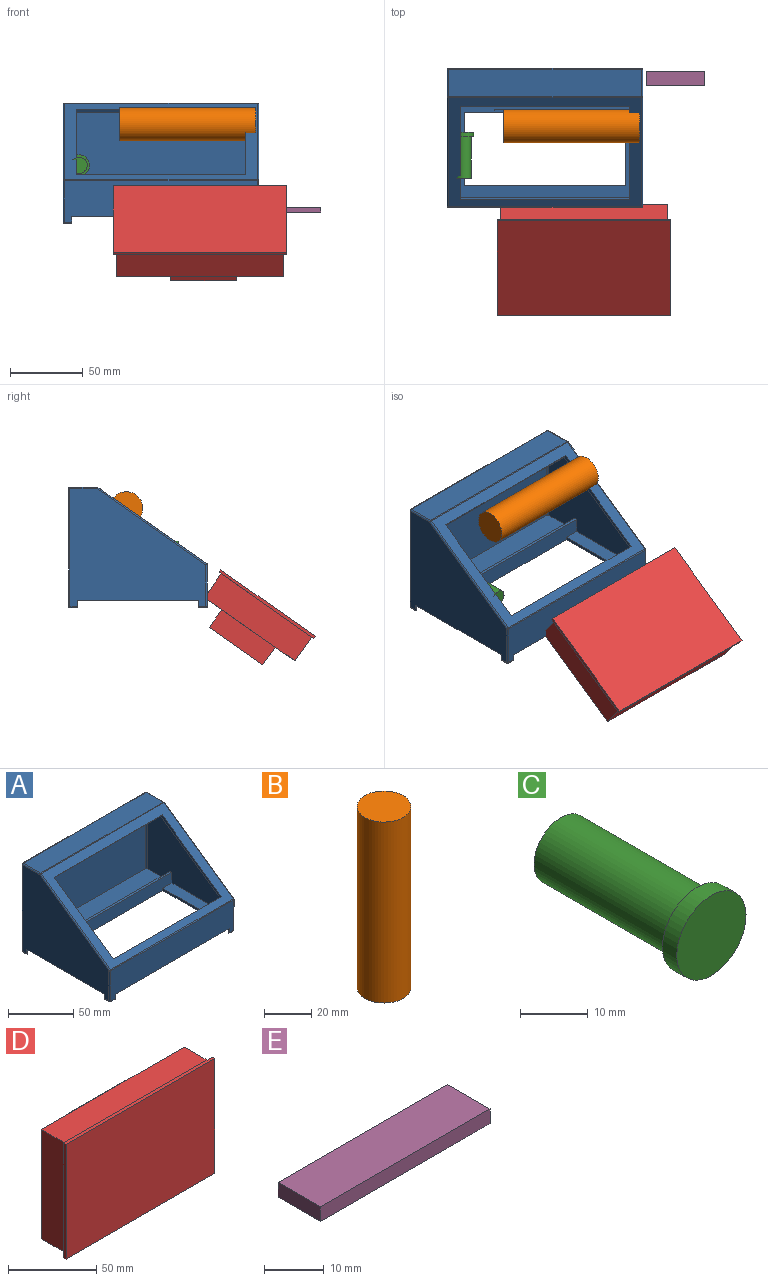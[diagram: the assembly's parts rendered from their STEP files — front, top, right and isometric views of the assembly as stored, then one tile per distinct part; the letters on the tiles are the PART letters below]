
ASSEMBLY  parts=5 mates=5
PART A: 92 faces, bbox 135x95.8x83.1 mm
  f0: plane 129x67.06mm, normal (0,-1,0), area 8477.5mm2, adj f3,f62,f63,f64,f88,f89,f90,f91
  f1: plane 133x81.06mm, normal (0,1,0), area 10115.7mm2, adj f3,f12,f32,f33,f34,f35,f75,f76
  f2: plane 90.77x68.06mm, normal (-1,0,0), area 4173.8mm2, adj f3,f6,f55,f56,f63,f65,f81,f85
  f3: plane 131x93.77mm, normal (0,0,1), area 6198.6mm2, adj f0,f1,f2,f5,f6,f63,f64,f81
  f4: plane 131x91.77mm, normal (0,0,-1), area 6379.9mm2, adj f7,f8,f21,f22,f61,f66,f81,f82
  f5: plane 90.77x68.06mm, normal (1,0,0), area 4193.8mm2, adj f3,f6,f55,f56,f64,f65
  f6: plane 131x15.35mm, normal (0,1,0), area 2010.7mm2, adj f2,f3,f5,f55
  f7: cylinder r=1mm len=8mm, axis (0,0,1), area 12.6mm2, adj f4,f21,f23,f61
  f8: cylinder r=1mm len=8mm, axis (0,0,-1), area 12.6mm2, adj f4,f9,f22,f61
  f9: plane 5x5mm, normal (0,0,-1), area 9.2mm2, adj f8,f15,f22,f27,f61,f69,f75
  f10: plane 5x5mm, normal (0,0,-1), area 9mm2, adj f14,f22,f28,f66,f70,f78
  f11: plane 133x28.48mm, normal (0,-1,0), area 3295.8mm2, adj f13,f41,f49,f50,f54,f78,f79,f80
  f12: cylinder r=1mm len=5mm, axis (-1,0,0), area 7.9mm2, adj f1,f15,f38,f75
  f13: cylinder r=1mm len=5mm, axis (-1,0,0), area 7.9mm2, adj f11,f14,f46,f78
  f14: plane 5x3mm, normal (0,1,0), area 15mm2, adj f10,f13,f28,f78
  f15: plane 5x3mm, normal (0,-1,0), area 15mm2, adj f9,f12,f27,f75
  f16: plane 93.77x81.06mm, normal (1,0,0), area 5291.7mm2, adj f17,f18,f32,f40,f48,f49,f72,f73
  f17: cylinder r=1mm len=5mm, axis (0,-1,0), area 7.9mm2, adj f16,f25,f37,f73
  f18: cylinder r=1mm len=5mm, axis (0,-1,0), area 7.9mm2, adj f16,f26,f45,f74
  f19: cylinder r=1mm len=5mm, axis (0,1,0), area 7.9mm2, adj f27,f31,f38,f69
  f20: cylinder r=1mm len=5mm, axis (0,1,0), area 7.9mm2, adj f28,f31,f46,f70
  f21: plane 90.77x8mm, normal (-1,0,0), area 558.6mm2, adj f4,f7,f23,f24,f66,f72,f73,f74
  f22: plane 90.77x8mm, normal (1,0,0), area 558.6mm2, adj f4,f8,f9,f10,f66,f69,f70,f71
  f23: plane 5x5mm, normal (0,0,-1), area 9.2mm2, adj f7,f21,f25,f61,f68,f73,f76
  f24: plane 5x5mm, normal (0,0,-1), area 9mm2, adj f21,f26,f66,f67,f74,f79
  f25: plane 5x3mm, normal (-1,0,0), area 15mm2, adj f17,f23,f68,f73
  f26: plane 5x3mm, normal (-1,0,0), area 15mm2, adj f18,f24,f67,f74
  f27: plane 5x3mm, normal (1,0,0), area 15mm2, adj f9,f15,f19,f69
  f28: plane 5x3mm, normal (1,0,0), area 15mm2, adj f10,f14,f20,f70
  f29: plane 133x75.09mm, normal (0,-0.57,0.82), area 3065.3mm2, adj f43,f48,f51,f54,f57,f58,f59,f60
  f30: plane 133x18.68mm, normal (0,0,1), area 2485.1mm2, adj f35,f40,f42,f43
  f31: plane 93.77x81.06mm, normal (-1,0,0), area 5291.7mm2, adj f19,f20,f34,f42,f50,f51,f69,f70
  f32: cylinder r=1mm len=81.06mm, axis (0,0,-1), area 127.3mm2, adj f1,f16,f36,f37
  f33: cylinder r=1mm len=5mm, axis (-1,0,0), area 7.9mm2, adj f1,f37,f68,f76
  f34: cylinder r=1mm len=81.06mm, axis (0,0,1), area 127.3mm2, adj f1,f31,f38,f39
  f35: cylinder r=1mm len=133mm, axis (-1,0,0), area 208.9mm2, adj f1,f30,f36,f39
  f36: sphere r=1mm, area 1.6mm2, adj f32,f35,f40
  f37: sphere r=1mm, area 1.6mm2, adj f17,f32,f33
  f38: sphere r=1mm, area 1.6mm2, adj f12,f19,f34
  f39: sphere r=1mm, area 1.6mm2, adj f34,f35,f42
  f40: cylinder r=1mm len=18.68mm, axis (0,1,0), area 29.3mm2, adj f16,f30,f36,f44
  f41: cylinder r=1mm len=5mm, axis (-1,0,0), area 7.9mm2, adj f11,f45,f67,f79
  f42: cylinder r=1mm len=18.68mm, axis (0,-1,0), area 29.3mm2, adj f30,f31,f39,f47
  f43: cylinder r=1mm len=133mm, axis (-1,0,0), area 81.2mm2, adj f29,f30,f44,f47
  f44: sphere r=1mm, area 0.6mm2, adj f40,f43,f48
  f45: sphere r=1mm, area 1.6mm2, adj f18,f41,f49
  f46: sphere r=1mm, area 1.6mm2, adj f13,f20,f50
  f47: sphere r=1mm, area 0.6mm2, adj f42,f43,f51
  f48: cylinder r=1mm len=75.66mm, axis (0,0.82,0.57), area 144mm2, adj f16,f29,f44,f52
  f49: cylinder r=1mm len=28.48mm, axis (0,0,1), area 44.7mm2, adj f11,f16,f45,f52
  f50: cylinder r=1mm len=28.48mm, axis (0,0,-1), area 44.7mm2, adj f11,f31,f46,f53
  f51: cylinder r=1mm len=75.66mm, axis (0,-0.82,-0.57), area 144mm2, adj f29,f31,f47,f53
  f52: sphere r=1mm, area 1mm2, adj f48,f49,f54
  f53: sphere r=1mm, area 1mm2, adj f50,f51,f54
  f54: cylinder r=1mm len=133mm, axis (-1,0,0), area 127.7mm2, adj f11,f29,f52,f53
  f55: plane 131x74.95mm, normal (0,0.57,-0.82), area 2859.7mm2, adj f2,f5,f6,f56,f57,f58,f59,f60
  f56: plane 131x0.23mm, normal (0,0.82,0.57), area 36.6mm2, adj f2,f5,f55,f65
  f57: plane 65.33x46.79mm, normal (-1,0,0), area 195mm2, adj f29,f55,f58,f60
  f58: plane 117x2.05mm, normal (0,0.82,0.57), area 292.5mm2, adj f29,f55,f57,f59
  f59: plane 65.33x46.79mm, normal (1,0,0), area 195mm2, adj f29,f55,f58,f60
  f60: plane 117x2.05mm, normal (0,-0.82,-0.57), area 292.5mm2, adj f29,f55,f57,f59
  f61: plane 129x8mm, normal (0,-1,0), area 786mm2, adj f4,f7,f8,f9,f23,f75,f76,f77
  f62: cylinder r=1mm len=131mm, axis (1,0,0), area 204.6mm2, adj f0,f63,f64,f65
  f63: cylinder r=1mm len=68.06mm, axis (0,0,1), area 106.3mm2, adj f0,f2,f3,f62
  f64: cylinder r=1mm len=68.06mm, axis (0,0,-1), area 106.3mm2, adj f0,f3,f5,f62
  f65: plane 131x15.98mm, normal (0,0,-1), area 2094mm2, adj f2,f5,f56,f62
  f66: plane 131x8mm, normal (0,1,0), area 802mm2, adj f4,f10,f21,f22,f24,f78,f79,f80
  f67: plane 5x3mm, normal (0,1,0), area 15mm2, adj f24,f26,f41,f79
  f68: plane 5x3mm, normal (0,-1,0), area 15mm2, adj f23,f25,f33,f76
  f69: plane 5x2mm, normal (0,-1,0), area 6.8mm2, adj f9,f19,f22,f27,f31,f71
  f70: plane 5x2mm, normal (0,1,0), area 6.8mm2, adj f10,f20,f22,f28,f31,f71
  f71: plane 83.77x2mm, normal (0,0,-1), area 167.5mm2, adj f22,f31,f69,f70
  f72: plane 83.77x2mm, normal (0,0,-1), area 167.5mm2, adj f16,f21,f73,f74
  f73: plane 5x2mm, normal (0,-1,0), area 6.8mm2, adj f16,f17,f21,f23,f25,f72
  f74: plane 5x2mm, normal (0,1,0), area 6.8mm2, adj f16,f18,f21,f24,f26,f72
  f75: plane 5x2mm, normal (1,0,0), area 6.8mm2, adj f1,f9,f12,f15,f61,f77
  f76: plane 5x2mm, normal (-1,0,0), area 6.8mm2, adj f1,f23,f33,f61,f68,f77
  f77: plane 123x2mm, normal (0,0,-1), area 246mm2, adj f1,f61,f75,f76
  f78: plane 5x2mm, normal (1,0,0), area 6.8mm2, adj f10,f11,f13,f14,f66,f80
  f79: plane 5x2mm, normal (-1,0,0), area 6.8mm2, adj f11,f24,f41,f66,f67,f80
  f80: plane 123x2mm, normal (0,0,-1), area 246mm2, adj f11,f66,f78,f79
  f81: plane 121x12mm, normal (0,-1,0), area 1228.2mm2, adj f2,f3,f4,f82,f84,f86,f87
  f82: plane 50.83x2mm, normal (1,0,0), area 101.7mm2, adj f3,f4,f81,f83
  f83: plane 111x2mm, normal (0,1,0), area 222mm2, adj f3,f4,f82,f84
  f84: plane 50.83x2mm, normal (-1,0,0), area 101.7mm2, adj f3,f4,f81,f83
  f85: plane 100.62x10mm, normal (0,1,0), area 1006.2mm2, adj f2,f3,f86,f87
  f86: plane 10x2mm, normal (-1,0,0), area 20mm2, adj f3,f81,f85,f87
  f87: plane 100.62x2mm, normal (0,0,1), area 201.2mm2, adj f2,f81,f85,f86
  f88: cylinder r=6.25mm len=12.5mm, axis (0,-1,0), area 78.5mm2, adj f0,f1
  f89: plane 5x2mm, normal (1,0,0), area 10mm2, adj f0,f1,f3,f91
  f90: plane 5x2mm, normal (-1,0,0), area 10mm2, adj f0,f1,f3,f91
  f91: plane 10x2mm, normal (0,0,-1), area 20mm2, adj f0,f1,f89,f90
PART B: 3 faces, bbox 22.9x22.9x94 mm
  f0: cylinder r=11.43mm len=93.98mm, axis (0,0,-1), area 6749.3mm2, adj f1,f2
  f1: plane 22.86x22.86mm, normal (0,0,1), area 410.4mm2, adj f0
  f2: plane 22.86x22.86mm, normal (0,0,-1), area 410.4mm2, adj f0
PART C: 5 faces, bbox 14.5x31.5x14.5 mm
  f0: cylinder r=5.65mm len=28.5mm, axis (0,1,0), area 1011.7mm2, adj f1,f4
  f1: plane 11.3x11.3mm, normal (0,1,0), area 100.3mm2, adj f0
  f2: cylinder r=7.25mm len=14.5mm, axis (0,1,0), area 136.7mm2, adj f3,f4
  f3: plane 14.5x14.5mm, normal (0,-1,0), area 165.1mm2, adj f2
  f4: plane 14.5x14.5mm, normal (0,1,0), area 64.8mm2, adj f0,f2
PART D: 16 faces, bbox 119.3x37x79.8 mm
  f0: plane 114.7x76.2mm, normal (0,1,0), area 6715.1mm2, adj f7,f8,f9,f10,f11,f12,f13,f14
  f1: plane 119.3x2mm, normal (0,0,1), area 238.6mm2, adj f2,f4,f5,f6
  f2: plane 79.8x2mm, normal (-1,0,0), area 159.6mm2, adj f1,f3,f5,f6
  f3: plane 119.3x2mm, normal (0,0,-1), area 238.6mm2, adj f2,f4,f5,f6
  f4: plane 79.8x2mm, normal (1,0,0), area 159.6mm2, adj f1,f3,f5,f6
  f5: plane 119.3x79.8mm, normal (0,-1,0), area 9520.1mm2, adj f1,f2,f3,f4
  f6: plane 119.3x79.8mm, normal (0,1,0), area 780mm2, adj f1,f2,f3,f4,f7,f8,f9,f10
  f7: plane 114.7x20mm, normal (0,0,-1), area 2294mm2, adj f0,f6,f8,f10
  f8: plane 76.2x20mm, normal (-1,0,0), area 1524mm2, adj f0,f6,f7,f9
  f9: plane 114.7x20mm, normal (0,0,1), area 2294mm2, adj f0,f6,f8,f10
  f10: plane 76.2x20mm, normal (1,0,0), area 1524mm2, adj f0,f6,f7,f9
  f11: plane 45x15mm, normal (0,0,1), area 675mm2, adj f0,f12,f14,f15
  f12: plane 45x15mm, normal (1,0,0), area 675mm2, adj f0,f11,f13,f15
  f13: plane 45x15mm, normal (0,0,-1), area 675mm2, adj f0,f12,f14,f15
  f14: plane 45x15mm, normal (-1,0,0), area 675mm2, adj f0,f11,f13,f15
  f15: plane 45x45mm, normal (0,1,0), area 2025mm2, adj f11,f12,f13,f14
PART E: 6 faces, bbox 40x10x3 mm
  f0: plane 40x3mm, normal (0,1,0), area 120mm2, adj f1,f3,f4,f5
  f1: plane 10x3mm, normal (-1,0,0), area 30mm2, adj f0,f2,f4,f5
  f2: plane 40x3mm, normal (0,-1,0), area 120mm2, adj f1,f3,f4,f5
  f3: plane 10x3mm, normal (1,0,0), area 30mm2, adj f0,f2,f4,f5
  f4: plane 40x10mm, normal (0,0,1), area 400mm2, adj f0,f1,f2,f3
  f5: plane 40x10mm, normal (0,0,-1), area 400mm2, adj f0,f1,f2,f3
PLACE A t=(-101,42.12,-64.88)mm
PLACE B rot(axis=(0,-1,0),90deg) t=(32,81.27,3.57)mm
PLACE C rot(axis=(1,0,0),180deg) t=(-83.26,45.43,-18.43)mm
PLACE D rot(axis=(-1,0,0),55deg) t=(-6.64,-15.41,-63.37)mm
PLACE E t=(81.39,137.81,-56.88)mm
MATE planar E.f0 <-> A.f61  axis (0,1,0) through (56.8,119.04,-55.38)mm
MATE planar A.f2 <-> B.f0  axis (-1,0,0) through (32,82.21,-25.53)mm
MATE planar D.f6 <-> A.f29  axis (0,0.57,-0.82) through (-6.64,-15.41,-63.37)mm
MATE cylindrical C.f0 <-> A.f88  axis (0,-1,0) through (-90,59.68,-24.63)mm
MATE planar E.f4 <-> A.f4  axis (0,0,1) through (56.8,114.04,-53.88)mm
